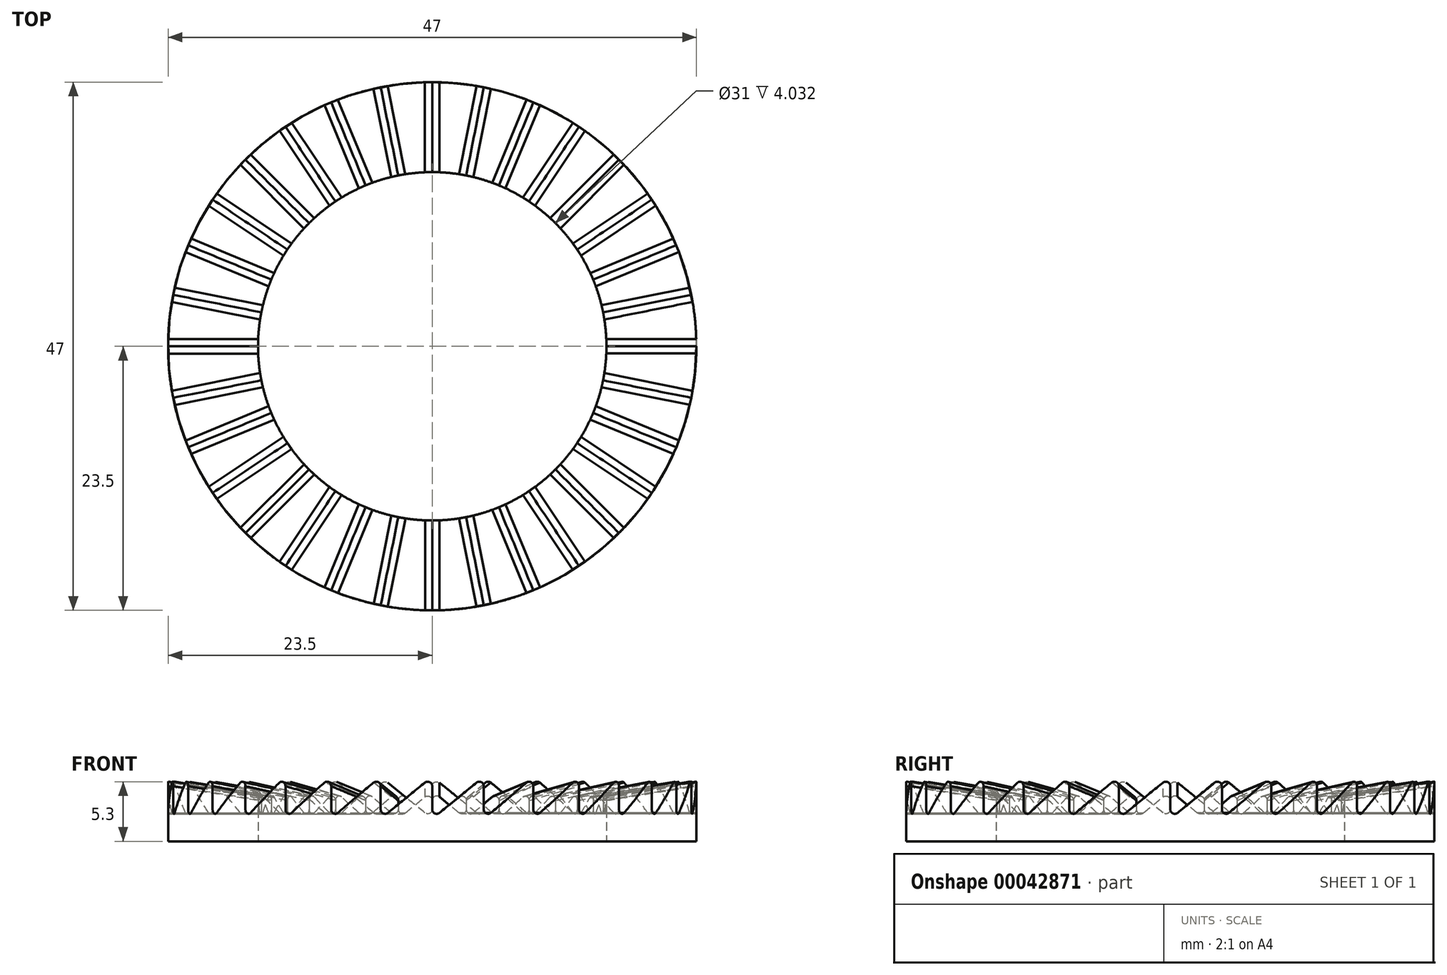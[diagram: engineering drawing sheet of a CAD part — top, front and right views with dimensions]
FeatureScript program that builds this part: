
annotation { "Feature Type Name" : "Feature", "Feature Type Description" : "" }
export const myFeature = defineFeature(function(context is Context, id is Id, definition is map)
    precondition{}
    {
        {
            var Q0;
            Q0=qCreatedBy(makeId("Top.planeOp"),FACE);
            var sketch = newSketch(context, id + "F0", { "sketchPlane" : qUnion([Q0])});
            skCircle(sketch, "E0", {"center": v(0, 0) * mm, "radius": 24 * mm});
            skCircle(sketch, "E1", {"center": v(0, 0) * mm, "radius": 25 * mm});
            skCircle(sketch, "E2", {"center": v(0, 0) * mm, "radius": 13 * mm});
            skCircle(sketch, "E3", {"center": v(0, 0) * mm, "radius": 15.5 * mm});
            skCircle(sketch, "E4", {"center": v(0, 0) * mm, "radius": 23.5 * mm});
            skCircle(sketch, "E5", {"center": v(0, 0) * mm, "radius": 12.5 * mm});
            skSolve(sketch);
        }
        {
            var Q0;
            Q0=makeQuery(id+"F0.imprint","IMPRINT",FACE,{"disambiguationData":[TD([[makeQuery(id+"F0.imprint","IMPRINT",EDGE,{"derivedFrom":sQuery(id+"F0.wireOp",EDGE,"E3")}),-1.0]])]});
            extrude(context, id + "F1", {"entities" : qUnion([Q0]), "depth" : 10 * mm});
        }
        {
            var Q0;
            Q0=qCreatedBy(makeId("Right.planeOp"),FACE);
            var sketch = newSketch(context, id + "F2", { "sketchPlane" : qUnion([Q0])});
            skLineSegment(sketch, "E6", {"start": v(0, 10) * mm, "end": v(0, 2) * mm});
            skLineSegment(sketch, "E7", {"start": v(0, 2) * mm, "end": v(9.8, 10) * mm});
            skLineSegment(sketch, "E8", {"start": v(0, 10) * mm, "end": v(9.8, 10) * mm});
            skSolve(sketch);
        }
        {
            var Q0;
            Q0=makeQuery(id+"F2.imprint","IMPRINT",FACE,{"disambiguationData":[TD([[makeQuery(id+"F2.imprint","IMPRINT",EDGE,{"derivedFrom":sQuery(id+"F2.wireOp",EDGE,"E6")}),1.0]])]});
            extrude(context, id + "F3", {"entities" : qUnion([Q0]), "depth" : 23.5 * mm});
        }
        {
            var Q0;
            Q0=makeQuery(id+"F3.opExtrude","SWEPT_BODY",BODY,{"disambiguationData":[OSD([sQuery(id+"F2.wireOp",EDGE,"E6"),sQuery(id+"F2.wireOp",EDGE,"E7"),sQuery(id+"F2.wireOp",EDGE,"E8")])]});
            var Q1;
            Q1=makeQuery(id+"F3.opExtrude","CAP_EDGE",EDGE,{"disambiguationData":[OSD([sQuery(id+"F2.wireOp",EDGE,"E6")])],"isStart":true});
            circularPattern(context, id + "F4", {"entities" : qUnion([Q0]), "axis" : qUnion([Q1]), "angle" : 11.25 * degree, "instanceCount" : round(32)});
        }
        {
            var Q0;
            Q0=makeQuery(id+"F3.opExtrude","SWEPT_BODY",BODY,{"disambiguationData":[OSD([sQuery(id+"F2.wireOp",EDGE,"E6"),sQuery(id+"F2.wireOp",EDGE,"E7"),sQuery(id+"F2.wireOp",EDGE,"E8")])]});
            var Q1;
            Q1=makeQuery(id+"F4.opPattern","COPY",BODY,{"derivedFrom":makeQuery(id+"F3.opExtrude","SWEPT_BODY",BODY,{"disambiguationData":[OSD([sQuery(id+"F2.wireOp",EDGE,"E6"),sQuery(id+"F2.wireOp",EDGE,"E7"),sQuery(id+"F2.wireOp",EDGE,"E8")])]}),"instanceName":"1"});
            var Q2;
            Q2=makeQuery(id+"F4.opPattern","COPY",BODY,{"derivedFrom":makeQuery(id+"F3.opExtrude","SWEPT_BODY",BODY,{"disambiguationData":[OSD([sQuery(id+"F2.wireOp",EDGE,"E6"),sQuery(id+"F2.wireOp",EDGE,"E7"),sQuery(id+"F2.wireOp",EDGE,"E8")])]}),"instanceName":"2"});
            var Q3;
            Q3=makeQuery(id+"F4.opPattern","COPY",BODY,{"derivedFrom":makeQuery(id+"F3.opExtrude","SWEPT_BODY",BODY,{"disambiguationData":[OSD([sQuery(id+"F2.wireOp",EDGE,"E6"),sQuery(id+"F2.wireOp",EDGE,"E7"),sQuery(id+"F2.wireOp",EDGE,"E8")])]}),"instanceName":"3"});
            var Q4;
            Q4=makeQuery(id+"F4.opPattern","COPY",BODY,{"derivedFrom":makeQuery(id+"F3.opExtrude","SWEPT_BODY",BODY,{"disambiguationData":[OSD([sQuery(id+"F2.wireOp",EDGE,"E6"),sQuery(id+"F2.wireOp",EDGE,"E7"),sQuery(id+"F2.wireOp",EDGE,"E8")])]}),"instanceName":"4"});
            var Q5;
            Q5=makeQuery(id+"F4.opPattern","COPY",BODY,{"derivedFrom":makeQuery(id+"F3.opExtrude","SWEPT_BODY",BODY,{"disambiguationData":[OSD([sQuery(id+"F2.wireOp",EDGE,"E6"),sQuery(id+"F2.wireOp",EDGE,"E7"),sQuery(id+"F2.wireOp",EDGE,"E8")])]}),"instanceName":"5"});
            var Q6;
            Q6=makeQuery(id+"F4.opPattern","COPY",BODY,{"derivedFrom":makeQuery(id+"F3.opExtrude","SWEPT_BODY",BODY,{"disambiguationData":[OSD([sQuery(id+"F2.wireOp",EDGE,"E6"),sQuery(id+"F2.wireOp",EDGE,"E7"),sQuery(id+"F2.wireOp",EDGE,"E8")])]}),"instanceName":"6"});
            var Q7;
            Q7=makeQuery(id+"F4.opPattern","COPY",BODY,{"derivedFrom":makeQuery(id+"F3.opExtrude","SWEPT_BODY",BODY,{"disambiguationData":[OSD([sQuery(id+"F2.wireOp",EDGE,"E6"),sQuery(id+"F2.wireOp",EDGE,"E7"),sQuery(id+"F2.wireOp",EDGE,"E8")])]}),"instanceName":"7"});
            var Q8;
            Q8=makeQuery(id+"F4.opPattern","COPY",BODY,{"derivedFrom":makeQuery(id+"F3.opExtrude","SWEPT_BODY",BODY,{"disambiguationData":[OSD([sQuery(id+"F2.wireOp",EDGE,"E6"),sQuery(id+"F2.wireOp",EDGE,"E7"),sQuery(id+"F2.wireOp",EDGE,"E8")])]}),"instanceName":"8"});
            var Q9;
            Q9=makeQuery(id+"F4.opPattern","COPY",BODY,{"derivedFrom":makeQuery(id+"F3.opExtrude","SWEPT_BODY",BODY,{"disambiguationData":[OSD([sQuery(id+"F2.wireOp",EDGE,"E6"),sQuery(id+"F2.wireOp",EDGE,"E7"),sQuery(id+"F2.wireOp",EDGE,"E8")])]}),"instanceName":"9"});
            var Q10;
            Q10=makeQuery(id+"F4.opPattern","COPY",BODY,{"derivedFrom":makeQuery(id+"F3.opExtrude","SWEPT_BODY",BODY,{"disambiguationData":[OSD([sQuery(id+"F2.wireOp",EDGE,"E6"),sQuery(id+"F2.wireOp",EDGE,"E7"),sQuery(id+"F2.wireOp",EDGE,"E8")])]}),"instanceName":"10"});
            var Q11;
            Q11=makeQuery(id+"F4.opPattern","COPY",BODY,{"derivedFrom":makeQuery(id+"F3.opExtrude","SWEPT_BODY",BODY,{"disambiguationData":[OSD([sQuery(id+"F2.wireOp",EDGE,"E6"),sQuery(id+"F2.wireOp",EDGE,"E7"),sQuery(id+"F2.wireOp",EDGE,"E8")])]}),"instanceName":"11"});
            var Q12;
            Q12=makeQuery(id+"F4.opPattern","COPY",BODY,{"derivedFrom":makeQuery(id+"F3.opExtrude","SWEPT_BODY",BODY,{"disambiguationData":[OSD([sQuery(id+"F2.wireOp",EDGE,"E6"),sQuery(id+"F2.wireOp",EDGE,"E7"),sQuery(id+"F2.wireOp",EDGE,"E8")])]}),"instanceName":"12"});
            var Q13;
            Q13=makeQuery(id+"F4.opPattern","COPY",BODY,{"derivedFrom":makeQuery(id+"F3.opExtrude","SWEPT_BODY",BODY,{"disambiguationData":[OSD([sQuery(id+"F2.wireOp",EDGE,"E6"),sQuery(id+"F2.wireOp",EDGE,"E7"),sQuery(id+"F2.wireOp",EDGE,"E8")])]}),"instanceName":"13"});
            var Q14;
            Q14=makeQuery(id+"F4.opPattern","COPY",BODY,{"derivedFrom":makeQuery(id+"F3.opExtrude","SWEPT_BODY",BODY,{"disambiguationData":[OSD([sQuery(id+"F2.wireOp",EDGE,"E6"),sQuery(id+"F2.wireOp",EDGE,"E7"),sQuery(id+"F2.wireOp",EDGE,"E8")])]}),"instanceName":"14"});
            var Q15;
            Q15=makeQuery(id+"F4.opPattern","COPY",BODY,{"derivedFrom":makeQuery(id+"F3.opExtrude","SWEPT_BODY",BODY,{"disambiguationData":[OSD([sQuery(id+"F2.wireOp",EDGE,"E6"),sQuery(id+"F2.wireOp",EDGE,"E7"),sQuery(id+"F2.wireOp",EDGE,"E8")])]}),"instanceName":"15"});
            var Q16;
            Q16=makeQuery(id+"F4.opPattern","COPY",BODY,{"derivedFrom":makeQuery(id+"F3.opExtrude","SWEPT_BODY",BODY,{"disambiguationData":[OSD([sQuery(id+"F2.wireOp",EDGE,"E6"),sQuery(id+"F2.wireOp",EDGE,"E7"),sQuery(id+"F2.wireOp",EDGE,"E8")])]}),"instanceName":"16"});
            var Q17;
            Q17=makeQuery(id+"F4.opPattern","COPY",BODY,{"derivedFrom":makeQuery(id+"F3.opExtrude","SWEPT_BODY",BODY,{"disambiguationData":[OSD([sQuery(id+"F2.wireOp",EDGE,"E6"),sQuery(id+"F2.wireOp",EDGE,"E7"),sQuery(id+"F2.wireOp",EDGE,"E8")])]}),"instanceName":"17"});
            var Q18;
            Q18=makeQuery(id+"F4.opPattern","COPY",BODY,{"derivedFrom":makeQuery(id+"F3.opExtrude","SWEPT_BODY",BODY,{"disambiguationData":[OSD([sQuery(id+"F2.wireOp",EDGE,"E6"),sQuery(id+"F2.wireOp",EDGE,"E7"),sQuery(id+"F2.wireOp",EDGE,"E8")])]}),"instanceName":"18"});
            var Q19;
            Q19=makeQuery(id+"F4.opPattern","COPY",BODY,{"derivedFrom":makeQuery(id+"F3.opExtrude","SWEPT_BODY",BODY,{"disambiguationData":[OSD([sQuery(id+"F2.wireOp",EDGE,"E6"),sQuery(id+"F2.wireOp",EDGE,"E7"),sQuery(id+"F2.wireOp",EDGE,"E8")])]}),"instanceName":"19"});
            var Q20;
            Q20=makeQuery(id+"F4.opPattern","COPY",BODY,{"derivedFrom":makeQuery(id+"F3.opExtrude","SWEPT_BODY",BODY,{"disambiguationData":[OSD([sQuery(id+"F2.wireOp",EDGE,"E6"),sQuery(id+"F2.wireOp",EDGE,"E7"),sQuery(id+"F2.wireOp",EDGE,"E8")])]}),"instanceName":"20"});
            var Q21;
            Q21=makeQuery(id+"F4.opPattern","COPY",BODY,{"derivedFrom":makeQuery(id+"F3.opExtrude","SWEPT_BODY",BODY,{"disambiguationData":[OSD([sQuery(id+"F2.wireOp",EDGE,"E6"),sQuery(id+"F2.wireOp",EDGE,"E7"),sQuery(id+"F2.wireOp",EDGE,"E8")])]}),"instanceName":"21"});
            var Q22;
            Q22=makeQuery(id+"F4.opPattern","COPY",BODY,{"derivedFrom":makeQuery(id+"F3.opExtrude","SWEPT_BODY",BODY,{"disambiguationData":[OSD([sQuery(id+"F2.wireOp",EDGE,"E6"),sQuery(id+"F2.wireOp",EDGE,"E7"),sQuery(id+"F2.wireOp",EDGE,"E8")])]}),"instanceName":"22"});
            var Q23;
            Q23=makeQuery(id+"F4.opPattern","COPY",BODY,{"derivedFrom":makeQuery(id+"F3.opExtrude","SWEPT_BODY",BODY,{"disambiguationData":[OSD([sQuery(id+"F2.wireOp",EDGE,"E6"),sQuery(id+"F2.wireOp",EDGE,"E7"),sQuery(id+"F2.wireOp",EDGE,"E8")])]}),"instanceName":"23"});
            var Q24;
            Q24=makeQuery(id+"F4.opPattern","COPY",BODY,{"derivedFrom":makeQuery(id+"F3.opExtrude","SWEPT_BODY",BODY,{"disambiguationData":[OSD([sQuery(id+"F2.wireOp",EDGE,"E6"),sQuery(id+"F2.wireOp",EDGE,"E7"),sQuery(id+"F2.wireOp",EDGE,"E8")])]}),"instanceName":"24"});
            var Q25;
            Q25=makeQuery(id+"F4.opPattern","COPY",BODY,{"derivedFrom":makeQuery(id+"F3.opExtrude","SWEPT_BODY",BODY,{"disambiguationData":[OSD([sQuery(id+"F2.wireOp",EDGE,"E6"),sQuery(id+"F2.wireOp",EDGE,"E7"),sQuery(id+"F2.wireOp",EDGE,"E8")])]}),"instanceName":"25"});
            var Q26;
            Q26=makeQuery(id+"F4.opPattern","COPY",BODY,{"derivedFrom":makeQuery(id+"F3.opExtrude","SWEPT_BODY",BODY,{"disambiguationData":[OSD([sQuery(id+"F2.wireOp",EDGE,"E6"),sQuery(id+"F2.wireOp",EDGE,"E7"),sQuery(id+"F2.wireOp",EDGE,"E8")])]}),"instanceName":"26"});
            var Q27;
            Q27=makeQuery(id+"F4.opPattern","COPY",BODY,{"derivedFrom":makeQuery(id+"F3.opExtrude","SWEPT_BODY",BODY,{"disambiguationData":[OSD([sQuery(id+"F2.wireOp",EDGE,"E6"),sQuery(id+"F2.wireOp",EDGE,"E7"),sQuery(id+"F2.wireOp",EDGE,"E8")])]}),"instanceName":"27"});
            var Q28;
            Q28=makeQuery(id+"F4.opPattern","COPY",BODY,{"derivedFrom":makeQuery(id+"F3.opExtrude","SWEPT_BODY",BODY,{"disambiguationData":[OSD([sQuery(id+"F2.wireOp",EDGE,"E6"),sQuery(id+"F2.wireOp",EDGE,"E7"),sQuery(id+"F2.wireOp",EDGE,"E8")])]}),"instanceName":"28"});
            var Q29;
            Q29=makeQuery(id+"F4.opPattern","COPY",BODY,{"derivedFrom":makeQuery(id+"F3.opExtrude","SWEPT_BODY",BODY,{"disambiguationData":[OSD([sQuery(id+"F2.wireOp",EDGE,"E6"),sQuery(id+"F2.wireOp",EDGE,"E7"),sQuery(id+"F2.wireOp",EDGE,"E8")])]}),"instanceName":"29"});
            var Q30;
            Q30=makeQuery(id+"F4.opPattern","COPY",BODY,{"derivedFrom":makeQuery(id+"F3.opExtrude","SWEPT_BODY",BODY,{"disambiguationData":[OSD([sQuery(id+"F2.wireOp",EDGE,"E6"),sQuery(id+"F2.wireOp",EDGE,"E7"),sQuery(id+"F2.wireOp",EDGE,"E8")])]}),"instanceName":"30"});
            var Q31;
            Q31=makeQuery(id+"F4.opPattern","COPY",BODY,{"derivedFrom":makeQuery(id+"F3.opExtrude","SWEPT_BODY",BODY,{"disambiguationData":[OSD([sQuery(id+"F2.wireOp",EDGE,"E6"),sQuery(id+"F2.wireOp",EDGE,"E7"),sQuery(id+"F2.wireOp",EDGE,"E8")])]}),"instanceName":"31"});
            booleanBodies(context, id + "F5", {"operationType" : BooleanOperationType.UNION, "tools" : qUnion([Q0, Q1, Q2, Q3, Q4, Q5, Q6, Q7, Q8, Q9, Q10, Q11, Q12, Q13, Q14, Q15, Q16, Q17, Q18, Q19, Q20, Q21, Q22, Q23, Q24, Q25, Q26, Q27, Q28, Q29, Q30, Q31])});
        }
        {
            var Q0;
            Q0=makeQuery(id+"F3.opExtrude","SWEPT_BODY",BODY,{"disambiguationData":[OSD([sQuery(id+"F2.wireOp",EDGE,"E6"),sQuery(id+"F2.wireOp",EDGE,"E7"),sQuery(id+"F2.wireOp",EDGE,"E8")])]});
            var Q1;
            Q1=makeQuery(id+"F1.opExtrude","SWEPT_BODY",BODY,{"disambiguationData":[OSD([sQuery(id+"F0.wireOp",EDGE,"E3"),sQuery(id+"F0.wireOp",EDGE,"E4")])]});
            booleanBodies(context, id + "F6", {"operationType" : BooleanOperationType.SUBTRACTION, "tools" : qUnion([Q0]), "targets" : qUnion([Q1])});
        }
        {
            var Q0;
            Q0=makeQuery(id+"F6.opBoolean","COPY",EDGE,{"derivedFrom":makeQuery(id+"F4.opPattern","COPY",EDGE,{"derivedFrom":makeQuery(id+"F3.opExtrude","SWEPT_EDGE",EDGE,{"disambiguationData":[OSD([sQuery(id+"F2.wireOp",EDGE,"E6"),sQuery(id+"F2.wireOp",EDGE,"E7")])]}),"instanceName":"6"})});
            var Q1;
            Q1=makeQuery(id+"F6.opBoolean","COPY",EDGE,{"derivedFrom":makeQuery(id+"F5.opBoolean","INTERSECT",EDGE,{"derivedFrom":[makeQuery(id+"F4.opPattern","COPY",FACE,{"derivedFrom":makeQuery(id+"F3.opExtrude","SWEPT_FACE",FACE,{"disambiguationData":[OSD([sQuery(id+"F2.wireOp",EDGE,"E6")])]}),"instanceName":"5"}),makeQuery(id+"F4.opPattern","COPY",FACE,{"derivedFrom":makeQuery(id+"F3.opExtrude","SWEPT_FACE",FACE,{"disambiguationData":[OSD([sQuery(id+"F2.wireOp",EDGE,"E7")])]}),"instanceName":"6"})]})});
            var Q2;
            Q2=makeQuery(id+"F6.opBoolean","COPY",EDGE,{"derivedFrom":makeQuery(id+"F4.opPattern","COPY",EDGE,{"derivedFrom":makeQuery(id+"F3.opExtrude","SWEPT_EDGE",EDGE,{"disambiguationData":[OSD([sQuery(id+"F2.wireOp",EDGE,"E6"),sQuery(id+"F2.wireOp",EDGE,"E7")])]}),"instanceName":"5"})});
            var Q3;
            Q3=makeQuery(id+"F6.opBoolean","COPY",EDGE,{"derivedFrom":makeQuery(id+"F5.opBoolean","INTERSECT",EDGE,{"derivedFrom":[makeQuery(id+"F4.opPattern","COPY",FACE,{"derivedFrom":makeQuery(id+"F3.opExtrude","SWEPT_FACE",FACE,{"disambiguationData":[OSD([sQuery(id+"F2.wireOp",EDGE,"E6")])]}),"instanceName":"4"}),makeQuery(id+"F4.opPattern","COPY",FACE,{"derivedFrom":makeQuery(id+"F3.opExtrude","SWEPT_FACE",FACE,{"disambiguationData":[OSD([sQuery(id+"F2.wireOp",EDGE,"E7")])]}),"instanceName":"5"})]})});
            var Q4;
            Q4=makeQuery(id+"F6.opBoolean","COPY",EDGE,{"derivedFrom":makeQuery(id+"F4.opPattern","COPY",EDGE,{"derivedFrom":makeQuery(id+"F3.opExtrude","SWEPT_EDGE",EDGE,{"disambiguationData":[OSD([sQuery(id+"F2.wireOp",EDGE,"E6"),sQuery(id+"F2.wireOp",EDGE,"E7")])]}),"instanceName":"4"})});
            var Q5;
            Q5=makeQuery(id+"F6.opBoolean","COPY",EDGE,{"derivedFrom":makeQuery(id+"F5.opBoolean","INTERSECT",EDGE,{"derivedFrom":[makeQuery(id+"F4.opPattern","COPY",FACE,{"derivedFrom":makeQuery(id+"F3.opExtrude","SWEPT_FACE",FACE,{"disambiguationData":[OSD([sQuery(id+"F2.wireOp",EDGE,"E6")])]}),"instanceName":"3"}),makeQuery(id+"F4.opPattern","COPY",FACE,{"derivedFrom":makeQuery(id+"F3.opExtrude","SWEPT_FACE",FACE,{"disambiguationData":[OSD([sQuery(id+"F2.wireOp",EDGE,"E7")])]}),"instanceName":"4"})]})});
            var Q6;
            Q6=makeQuery(id+"F6.opBoolean","COPY",EDGE,{"derivedFrom":makeQuery(id+"F4.opPattern","COPY",EDGE,{"derivedFrom":makeQuery(id+"F3.opExtrude","SWEPT_EDGE",EDGE,{"disambiguationData":[OSD([sQuery(id+"F2.wireOp",EDGE,"E6"),sQuery(id+"F2.wireOp",EDGE,"E7")])]}),"instanceName":"3"})});
            var Q7;
            Q7=makeQuery(id+"F6.opBoolean","COPY",EDGE,{"derivedFrom":makeQuery(id+"F5.opBoolean","INTERSECT",EDGE,{"derivedFrom":[makeQuery(id+"F4.opPattern","COPY",FACE,{"derivedFrom":makeQuery(id+"F3.opExtrude","SWEPT_FACE",FACE,{"disambiguationData":[OSD([sQuery(id+"F2.wireOp",EDGE,"E6")])]}),"instanceName":"2"}),makeQuery(id+"F4.opPattern","COPY",FACE,{"derivedFrom":makeQuery(id+"F3.opExtrude","SWEPT_FACE",FACE,{"disambiguationData":[OSD([sQuery(id+"F2.wireOp",EDGE,"E7")])]}),"instanceName":"3"})]})});
            var Q8;
            Q8=makeQuery(id+"F6.opBoolean","COPY",EDGE,{"derivedFrom":makeQuery(id+"F4.opPattern","COPY",EDGE,{"derivedFrom":makeQuery(id+"F3.opExtrude","SWEPT_EDGE",EDGE,{"disambiguationData":[OSD([sQuery(id+"F2.wireOp",EDGE,"E6"),sQuery(id+"F2.wireOp",EDGE,"E7")])]}),"instanceName":"2"})});
            var Q9;
            Q9=makeQuery(id+"F6.opBoolean","COPY",EDGE,{"derivedFrom":makeQuery(id+"F5.opBoolean","INTERSECT",EDGE,{"derivedFrom":[makeQuery(id+"F4.opPattern","COPY",FACE,{"derivedFrom":makeQuery(id+"F3.opExtrude","SWEPT_FACE",FACE,{"disambiguationData":[OSD([sQuery(id+"F2.wireOp",EDGE,"E6")])]}),"instanceName":"1"}),makeQuery(id+"F4.opPattern","COPY",FACE,{"derivedFrom":makeQuery(id+"F3.opExtrude","SWEPT_FACE",FACE,{"disambiguationData":[OSD([sQuery(id+"F2.wireOp",EDGE,"E7")])]}),"instanceName":"2"})]})});
            var Q10;
            Q10=makeQuery(id+"F6.opBoolean","COPY",EDGE,{"derivedFrom":makeQuery(id+"F4.opPattern","COPY",EDGE,{"derivedFrom":makeQuery(id+"F3.opExtrude","SWEPT_EDGE",EDGE,{"disambiguationData":[OSD([sQuery(id+"F2.wireOp",EDGE,"E6"),sQuery(id+"F2.wireOp",EDGE,"E7")])]}),"instanceName":"1"})});
            var Q11;
            Q11=makeQuery(id+"F6.opBoolean","COPY",EDGE,{"derivedFrom":makeQuery(id+"F3.opExtrude","SWEPT_EDGE",EDGE,{"disambiguationData":[OSD([sQuery(id+"F2.wireOp",EDGE,"E6"),sQuery(id+"F2.wireOp",EDGE,"E7")])]})});
            var Q12;
            Q12=makeQuery(id+"F6.opBoolean","COPY",EDGE,{"derivedFrom":makeQuery(id+"F5.opBoolean","INTERSECT",EDGE,{"derivedFrom":[makeQuery(id+"F3.opExtrude","SWEPT_FACE",FACE,{"disambiguationData":[OSD([sQuery(id+"F2.wireOp",EDGE,"E6")])]}),makeQuery(id+"F4.opPattern","COPY",FACE,{"derivedFrom":makeQuery(id+"F3.opExtrude","SWEPT_FACE",FACE,{"disambiguationData":[OSD([sQuery(id+"F2.wireOp",EDGE,"E7")])]}),"instanceName":"1"})]})});
            var Q13;
            {var subQ0=sQuery(id+"F2.wireOp",EDGE,"E7");var subQ1=sQuery(id+"F2.wireOp",EDGE,"E6");Q13=makeQuery(id+"F6.opBoolean","COPY",EDGE,{"derivedFrom":makeQuery(id+"F5.opBoolean","INTERSECT",EDGE,{"derivedFrom":[makeQuery(id+"F3.opExtrude","SWEPT_FACE",FACE,{"disambiguationData":[OSD([subQ0])]}),makeQuery(id+"F4.opPattern","COPY",FACE,{"derivedFrom":makeQuery(id+"F3.opExtrude","CAP_FACE",FACE,{"disambiguationData":[OSD([subQ1,subQ0,sQuery(id+"F2.wireOp",EDGE,"E8")])],"isStart":true}),"instanceName":"23"}),makeQuery(id+"F4.opPattern","COPY",FACE,{"derivedFrom":makeQuery(id+"F3.opExtrude","SWEPT_FACE",FACE,{"disambiguationData":[OSD([subQ1])]}),"instanceName":"31"})]})});}
            var Q14;
            Q14=makeQuery(id+"F6.opBoolean","COPY",EDGE,{"derivedFrom":makeQuery(id+"F4.opPattern","COPY",EDGE,{"derivedFrom":makeQuery(id+"F3.opExtrude","SWEPT_EDGE",EDGE,{"disambiguationData":[OSD([sQuery(id+"F2.wireOp",EDGE,"E6"),sQuery(id+"F2.wireOp",EDGE,"E7")])]}),"instanceName":"31"})});
            var Q15;
            Q15=makeQuery(id+"F6.opBoolean","COPY",EDGE,{"derivedFrom":makeQuery(id+"F5.opBoolean","INTERSECT",EDGE,{"derivedFrom":[makeQuery(id+"F4.opPattern","COPY",FACE,{"derivedFrom":makeQuery(id+"F3.opExtrude","SWEPT_FACE",FACE,{"disambiguationData":[OSD([sQuery(id+"F2.wireOp",EDGE,"E6")])]}),"instanceName":"30"}),makeQuery(id+"F4.opPattern","COPY",FACE,{"derivedFrom":makeQuery(id+"F3.opExtrude","SWEPT_FACE",FACE,{"disambiguationData":[OSD([sQuery(id+"F2.wireOp",EDGE,"E7")])]}),"instanceName":"31"})]})});
            var Q16;
            Q16=makeQuery(id+"F6.opBoolean","COPY",EDGE,{"derivedFrom":makeQuery(id+"F5.opBoolean","INTERSECT",EDGE,{"derivedFrom":[makeQuery(id+"F4.opPattern","COPY",FACE,{"derivedFrom":makeQuery(id+"F3.opExtrude","SWEPT_FACE",FACE,{"disambiguationData":[OSD([sQuery(id+"F2.wireOp",EDGE,"E6")])]}),"instanceName":"29"}),makeQuery(id+"F4.opPattern","COPY",FACE,{"derivedFrom":makeQuery(id+"F3.opExtrude","SWEPT_FACE",FACE,{"disambiguationData":[OSD([sQuery(id+"F2.wireOp",EDGE,"E7")])]}),"instanceName":"30"})]})});
            var Q17;
            Q17=makeQuery(id+"F6.opBoolean","COPY",EDGE,{"derivedFrom":makeQuery(id+"F4.opPattern","COPY",EDGE,{"derivedFrom":makeQuery(id+"F3.opExtrude","SWEPT_EDGE",EDGE,{"disambiguationData":[OSD([sQuery(id+"F2.wireOp",EDGE,"E6"),sQuery(id+"F2.wireOp",EDGE,"E7")])]}),"instanceName":"29"})});
            var Q18;
            Q18=makeQuery(id+"F6.opBoolean","COPY",EDGE,{"derivedFrom":makeQuery(id+"F4.opPattern","COPY",EDGE,{"derivedFrom":makeQuery(id+"F3.opExtrude","SWEPT_EDGE",EDGE,{"disambiguationData":[OSD([sQuery(id+"F2.wireOp",EDGE,"E6"),sQuery(id+"F2.wireOp",EDGE,"E7")])]}),"instanceName":"30"})});
            var Q19;
            Q19=makeQuery(id+"F6.opBoolean","COPY",EDGE,{"derivedFrom":makeQuery(id+"F5.opBoolean","INTERSECT",EDGE,{"derivedFrom":[makeQuery(id+"F4.opPattern","COPY",FACE,{"derivedFrom":makeQuery(id+"F3.opExtrude","SWEPT_FACE",FACE,{"disambiguationData":[OSD([sQuery(id+"F2.wireOp",EDGE,"E6")])]}),"instanceName":"28"}),makeQuery(id+"F4.opPattern","COPY",FACE,{"derivedFrom":makeQuery(id+"F3.opExtrude","SWEPT_FACE",FACE,{"disambiguationData":[OSD([sQuery(id+"F2.wireOp",EDGE,"E7")])]}),"instanceName":"29"})]})});
            var Q20;
            Q20=makeQuery(id+"F6.opBoolean","COPY",EDGE,{"derivedFrom":makeQuery(id+"F4.opPattern","COPY",EDGE,{"derivedFrom":makeQuery(id+"F3.opExtrude","SWEPT_EDGE",EDGE,{"disambiguationData":[OSD([sQuery(id+"F2.wireOp",EDGE,"E6"),sQuery(id+"F2.wireOp",EDGE,"E7")])]}),"instanceName":"28"})});
            var Q21;
            Q21=makeQuery(id+"F6.opBoolean","COPY",EDGE,{"derivedFrom":makeQuery(id+"F5.opBoolean","INTERSECT",EDGE,{"derivedFrom":[makeQuery(id+"F4.opPattern","COPY",FACE,{"derivedFrom":makeQuery(id+"F3.opExtrude","SWEPT_FACE",FACE,{"disambiguationData":[OSD([sQuery(id+"F2.wireOp",EDGE,"E6")])]}),"instanceName":"27"}),makeQuery(id+"F4.opPattern","COPY",FACE,{"derivedFrom":makeQuery(id+"F3.opExtrude","SWEPT_FACE",FACE,{"disambiguationData":[OSD([sQuery(id+"F2.wireOp",EDGE,"E7")])]}),"instanceName":"28"})]})});
            var Q22;
            Q22=makeQuery(id+"F6.opBoolean","COPY",EDGE,{"derivedFrom":makeQuery(id+"F4.opPattern","COPY",EDGE,{"derivedFrom":makeQuery(id+"F3.opExtrude","SWEPT_EDGE",EDGE,{"disambiguationData":[OSD([sQuery(id+"F2.wireOp",EDGE,"E6"),sQuery(id+"F2.wireOp",EDGE,"E7")])]}),"instanceName":"27"})});
            var Q23;
            Q23=makeQuery(id+"F6.opBoolean","COPY",EDGE,{"derivedFrom":makeQuery(id+"F5.opBoolean","INTERSECT",EDGE,{"derivedFrom":[makeQuery(id+"F4.opPattern","COPY",FACE,{"derivedFrom":makeQuery(id+"F3.opExtrude","SWEPT_FACE",FACE,{"disambiguationData":[OSD([sQuery(id+"F2.wireOp",EDGE,"E6")])]}),"instanceName":"26"}),makeQuery(id+"F4.opPattern","COPY",FACE,{"derivedFrom":makeQuery(id+"F3.opExtrude","SWEPT_FACE",FACE,{"disambiguationData":[OSD([sQuery(id+"F2.wireOp",EDGE,"E7")])]}),"instanceName":"27"})]})});
            var Q24;
            Q24=makeQuery(id+"F6.opBoolean","COPY",EDGE,{"derivedFrom":makeQuery(id+"F4.opPattern","COPY",EDGE,{"derivedFrom":makeQuery(id+"F3.opExtrude","SWEPT_EDGE",EDGE,{"disambiguationData":[OSD([sQuery(id+"F2.wireOp",EDGE,"E6"),sQuery(id+"F2.wireOp",EDGE,"E7")])]}),"instanceName":"26"})});
            var Q25;
            Q25=makeQuery(id+"F6.opBoolean","COPY",EDGE,{"derivedFrom":makeQuery(id+"F5.opBoolean","INTERSECT",EDGE,{"derivedFrom":[makeQuery(id+"F4.opPattern","COPY",FACE,{"derivedFrom":makeQuery(id+"F3.opExtrude","SWEPT_FACE",FACE,{"disambiguationData":[OSD([sQuery(id+"F2.wireOp",EDGE,"E6")])]}),"instanceName":"25"}),makeQuery(id+"F4.opPattern","COPY",FACE,{"derivedFrom":makeQuery(id+"F3.opExtrude","SWEPT_FACE",FACE,{"disambiguationData":[OSD([sQuery(id+"F2.wireOp",EDGE,"E7")])]}),"instanceName":"26"})]})});
            var Q26;
            Q26=makeQuery(id+"F6.opBoolean","COPY",EDGE,{"derivedFrom":makeQuery(id+"F4.opPattern","COPY",EDGE,{"derivedFrom":makeQuery(id+"F3.opExtrude","SWEPT_EDGE",EDGE,{"disambiguationData":[OSD([sQuery(id+"F2.wireOp",EDGE,"E6"),sQuery(id+"F2.wireOp",EDGE,"E7")])]}),"instanceName":"25"})});
            var Q27;
            Q27=makeQuery(id+"F6.opBoolean","COPY",EDGE,{"derivedFrom":makeQuery(id+"F5.opBoolean","INTERSECT",EDGE,{"derivedFrom":[makeQuery(id+"F4.opPattern","COPY",FACE,{"derivedFrom":makeQuery(id+"F3.opExtrude","SWEPT_FACE",FACE,{"disambiguationData":[OSD([sQuery(id+"F2.wireOp",EDGE,"E6")])]}),"instanceName":"24"}),makeQuery(id+"F4.opPattern","COPY",FACE,{"derivedFrom":makeQuery(id+"F3.opExtrude","SWEPT_FACE",FACE,{"disambiguationData":[OSD([sQuery(id+"F2.wireOp",EDGE,"E7")])]}),"instanceName":"25"})]})});
            var Q28;
            Q28=makeQuery(id+"F6.opBoolean","COPY",EDGE,{"derivedFrom":makeQuery(id+"F4.opPattern","COPY",EDGE,{"derivedFrom":makeQuery(id+"F3.opExtrude","SWEPT_EDGE",EDGE,{"disambiguationData":[OSD([sQuery(id+"F2.wireOp",EDGE,"E6"),sQuery(id+"F2.wireOp",EDGE,"E7")])]}),"instanceName":"24"})});
            var Q29;
            Q29=makeQuery(id+"F6.opBoolean","COPY",EDGE,{"derivedFrom":makeQuery(id+"F5.opBoolean","INTERSECT",EDGE,{"derivedFrom":[makeQuery(id+"F4.opPattern","COPY",FACE,{"derivedFrom":makeQuery(id+"F3.opExtrude","SWEPT_FACE",FACE,{"disambiguationData":[OSD([sQuery(id+"F2.wireOp",EDGE,"E6")])]}),"instanceName":"23"}),makeQuery(id+"F4.opPattern","COPY",FACE,{"derivedFrom":makeQuery(id+"F3.opExtrude","SWEPT_FACE",FACE,{"disambiguationData":[OSD([sQuery(id+"F2.wireOp",EDGE,"E7")])]}),"instanceName":"24"})]})});
            var Q30;
            Q30=makeQuery(id+"F6.opBoolean","COPY",EDGE,{"derivedFrom":makeQuery(id+"F4.opPattern","COPY",EDGE,{"derivedFrom":makeQuery(id+"F3.opExtrude","SWEPT_EDGE",EDGE,{"disambiguationData":[OSD([sQuery(id+"F2.wireOp",EDGE,"E6"),sQuery(id+"F2.wireOp",EDGE,"E7")])]}),"instanceName":"23"})});
            var Q31;
            Q31=makeQuery(id+"F6.opBoolean","COPY",EDGE,{"derivedFrom":makeQuery(id+"F5.opBoolean","INTERSECT",EDGE,{"derivedFrom":[makeQuery(id+"F4.opPattern","COPY",FACE,{"derivedFrom":makeQuery(id+"F3.opExtrude","SWEPT_FACE",FACE,{"disambiguationData":[OSD([sQuery(id+"F2.wireOp",EDGE,"E6")])]}),"instanceName":"22"}),makeQuery(id+"F4.opPattern","COPY",FACE,{"derivedFrom":makeQuery(id+"F3.opExtrude","SWEPT_FACE",FACE,{"disambiguationData":[OSD([sQuery(id+"F2.wireOp",EDGE,"E7")])]}),"instanceName":"23"})]})});
            var Q32;
            Q32=makeQuery(id+"F6.opBoolean","COPY",EDGE,{"derivedFrom":makeQuery(id+"F4.opPattern","COPY",EDGE,{"derivedFrom":makeQuery(id+"F3.opExtrude","SWEPT_EDGE",EDGE,{"disambiguationData":[OSD([sQuery(id+"F2.wireOp",EDGE,"E6"),sQuery(id+"F2.wireOp",EDGE,"E7")])]}),"instanceName":"22"})});
            var Q33;
            Q33=makeQuery(id+"F6.opBoolean","COPY",EDGE,{"derivedFrom":makeQuery(id+"F5.opBoolean","INTERSECT",EDGE,{"derivedFrom":[makeQuery(id+"F4.opPattern","COPY",FACE,{"derivedFrom":makeQuery(id+"F3.opExtrude","SWEPT_FACE",FACE,{"disambiguationData":[OSD([sQuery(id+"F2.wireOp",EDGE,"E6")])]}),"instanceName":"21"}),makeQuery(id+"F4.opPattern","COPY",FACE,{"derivedFrom":makeQuery(id+"F3.opExtrude","SWEPT_FACE",FACE,{"disambiguationData":[OSD([sQuery(id+"F2.wireOp",EDGE,"E7")])]}),"instanceName":"22"})]})});
            var Q34;
            Q34=makeQuery(id+"F6.opBoolean","COPY",EDGE,{"derivedFrom":makeQuery(id+"F4.opPattern","COPY",EDGE,{"derivedFrom":makeQuery(id+"F3.opExtrude","SWEPT_EDGE",EDGE,{"disambiguationData":[OSD([sQuery(id+"F2.wireOp",EDGE,"E6"),sQuery(id+"F2.wireOp",EDGE,"E7")])]}),"instanceName":"21"})});
            var Q35;
            Q35=makeQuery(id+"F6.opBoolean","COPY",EDGE,{"derivedFrom":makeQuery(id+"F5.opBoolean","INTERSECT",EDGE,{"derivedFrom":[makeQuery(id+"F4.opPattern","COPY",FACE,{"derivedFrom":makeQuery(id+"F3.opExtrude","SWEPT_FACE",FACE,{"disambiguationData":[OSD([sQuery(id+"F2.wireOp",EDGE,"E6")])]}),"instanceName":"20"}),makeQuery(id+"F4.opPattern","COPY",FACE,{"derivedFrom":makeQuery(id+"F3.opExtrude","SWEPT_FACE",FACE,{"disambiguationData":[OSD([sQuery(id+"F2.wireOp",EDGE,"E7")])]}),"instanceName":"21"})]})});
            var Q36;
            Q36=makeQuery(id+"F6.opBoolean","COPY",EDGE,{"derivedFrom":makeQuery(id+"F4.opPattern","COPY",EDGE,{"derivedFrom":makeQuery(id+"F3.opExtrude","SWEPT_EDGE",EDGE,{"disambiguationData":[OSD([sQuery(id+"F2.wireOp",EDGE,"E6"),sQuery(id+"F2.wireOp",EDGE,"E7")])]}),"instanceName":"20"})});
            var Q37;
            Q37=makeQuery(id+"F6.opBoolean","COPY",EDGE,{"derivedFrom":makeQuery(id+"F5.opBoolean","INTERSECT",EDGE,{"derivedFrom":[makeQuery(id+"F4.opPattern","COPY",FACE,{"derivedFrom":makeQuery(id+"F3.opExtrude","SWEPT_FACE",FACE,{"disambiguationData":[OSD([sQuery(id+"F2.wireOp",EDGE,"E6")])]}),"instanceName":"19"}),makeQuery(id+"F4.opPattern","COPY",FACE,{"derivedFrom":makeQuery(id+"F3.opExtrude","SWEPT_FACE",FACE,{"disambiguationData":[OSD([sQuery(id+"F2.wireOp",EDGE,"E7")])]}),"instanceName":"20"})]})});
            var Q38;
            Q38=makeQuery(id+"F6.opBoolean","COPY",EDGE,{"derivedFrom":makeQuery(id+"F4.opPattern","COPY",EDGE,{"derivedFrom":makeQuery(id+"F3.opExtrude","SWEPT_EDGE",EDGE,{"disambiguationData":[OSD([sQuery(id+"F2.wireOp",EDGE,"E6"),sQuery(id+"F2.wireOp",EDGE,"E7")])]}),"instanceName":"19"})});
            var Q39;
            Q39=makeQuery(id+"F6.opBoolean","COPY",EDGE,{"derivedFrom":makeQuery(id+"F5.opBoolean","INTERSECT",EDGE,{"derivedFrom":[makeQuery(id+"F4.opPattern","COPY",FACE,{"derivedFrom":makeQuery(id+"F3.opExtrude","SWEPT_FACE",FACE,{"disambiguationData":[OSD([sQuery(id+"F2.wireOp",EDGE,"E6")])]}),"instanceName":"18"}),makeQuery(id+"F4.opPattern","COPY",FACE,{"derivedFrom":makeQuery(id+"F3.opExtrude","SWEPT_FACE",FACE,{"disambiguationData":[OSD([sQuery(id+"F2.wireOp",EDGE,"E7")])]}),"instanceName":"19"})]})});
            var Q40;
            Q40=makeQuery(id+"F6.opBoolean","COPY",EDGE,{"derivedFrom":makeQuery(id+"F4.opPattern","COPY",EDGE,{"derivedFrom":makeQuery(id+"F3.opExtrude","SWEPT_EDGE",EDGE,{"disambiguationData":[OSD([sQuery(id+"F2.wireOp",EDGE,"E6"),sQuery(id+"F2.wireOp",EDGE,"E7")])]}),"instanceName":"18"})});
            var Q41;
            Q41=makeQuery(id+"F6.opBoolean","COPY",EDGE,{"derivedFrom":makeQuery(id+"F5.opBoolean","INTERSECT",EDGE,{"derivedFrom":[makeQuery(id+"F4.opPattern","COPY",FACE,{"derivedFrom":makeQuery(id+"F3.opExtrude","SWEPT_FACE",FACE,{"disambiguationData":[OSD([sQuery(id+"F2.wireOp",EDGE,"E6")])]}),"instanceName":"17"}),makeQuery(id+"F4.opPattern","COPY",FACE,{"derivedFrom":makeQuery(id+"F3.opExtrude","SWEPT_FACE",FACE,{"disambiguationData":[OSD([sQuery(id+"F2.wireOp",EDGE,"E7")])]}),"instanceName":"18"})]})});
            var Q42;
            Q42=makeQuery(id+"F6.opBoolean","COPY",EDGE,{"derivedFrom":makeQuery(id+"F4.opPattern","COPY",EDGE,{"derivedFrom":makeQuery(id+"F3.opExtrude","SWEPT_EDGE",EDGE,{"disambiguationData":[OSD([sQuery(id+"F2.wireOp",EDGE,"E6"),sQuery(id+"F2.wireOp",EDGE,"E7")])]}),"instanceName":"17"})});
            var Q43;
            Q43=makeQuery(id+"F6.opBoolean","COPY",EDGE,{"derivedFrom":makeQuery(id+"F5.opBoolean","INTERSECT",EDGE,{"derivedFrom":[makeQuery(id+"F4.opPattern","COPY",FACE,{"derivedFrom":makeQuery(id+"F3.opExtrude","SWEPT_FACE",FACE,{"disambiguationData":[OSD([sQuery(id+"F2.wireOp",EDGE,"E6")])]}),"instanceName":"16"}),makeQuery(id+"F4.opPattern","COPY",FACE,{"derivedFrom":makeQuery(id+"F3.opExtrude","SWEPT_FACE",FACE,{"disambiguationData":[OSD([sQuery(id+"F2.wireOp",EDGE,"E7")])]}),"instanceName":"17"})]})});
            var Q44;
            Q44=makeQuery(id+"F6.opBoolean","COPY",EDGE,{"derivedFrom":makeQuery(id+"F4.opPattern","COPY",EDGE,{"derivedFrom":makeQuery(id+"F3.opExtrude","SWEPT_EDGE",EDGE,{"disambiguationData":[OSD([sQuery(id+"F2.wireOp",EDGE,"E6"),sQuery(id+"F2.wireOp",EDGE,"E7")])]}),"instanceName":"16"})});
            var Q45;
            Q45=makeQuery(id+"F6.opBoolean","COPY",EDGE,{"derivedFrom":makeQuery(id+"F5.opBoolean","INTERSECT",EDGE,{"derivedFrom":[makeQuery(id+"F4.opPattern","COPY",FACE,{"derivedFrom":makeQuery(id+"F3.opExtrude","SWEPT_FACE",FACE,{"disambiguationData":[OSD([sQuery(id+"F2.wireOp",EDGE,"E6")])]}),"instanceName":"15"}),makeQuery(id+"F4.opPattern","COPY",FACE,{"derivedFrom":makeQuery(id+"F3.opExtrude","SWEPT_FACE",FACE,{"disambiguationData":[OSD([sQuery(id+"F2.wireOp",EDGE,"E7")])]}),"instanceName":"16"})]})});
            var Q46;
            Q46=makeQuery(id+"F6.opBoolean","COPY",EDGE,{"derivedFrom":makeQuery(id+"F4.opPattern","COPY",EDGE,{"derivedFrom":makeQuery(id+"F3.opExtrude","SWEPT_EDGE",EDGE,{"disambiguationData":[OSD([sQuery(id+"F2.wireOp",EDGE,"E6"),sQuery(id+"F2.wireOp",EDGE,"E7")])]}),"instanceName":"15"})});
            var Q47;
            Q47=makeQuery(id+"F6.opBoolean","COPY",EDGE,{"derivedFrom":makeQuery(id+"F4.opPattern","COPY",EDGE,{"derivedFrom":makeQuery(id+"F3.opExtrude","SWEPT_EDGE",EDGE,{"disambiguationData":[OSD([sQuery(id+"F2.wireOp",EDGE,"E6"),sQuery(id+"F2.wireOp",EDGE,"E7")])]}),"instanceName":"14"})});
            var Q48;
            Q48=makeQuery(id+"F6.opBoolean","COPY",EDGE,{"derivedFrom":makeQuery(id+"F5.opBoolean","INTERSECT",EDGE,{"derivedFrom":[makeQuery(id+"F4.opPattern","COPY",FACE,{"derivedFrom":makeQuery(id+"F3.opExtrude","SWEPT_FACE",FACE,{"disambiguationData":[OSD([sQuery(id+"F2.wireOp",EDGE,"E6")])]}),"instanceName":"15"}),makeQuery(id+"F4.opPattern","COPY",FACE,{"derivedFrom":makeQuery(id+"F3.opExtrude","SWEPT_FACE",FACE,{"disambiguationData":[OSD([sQuery(id+"F2.wireOp",EDGE,"E7")])]}),"instanceName":"16"})]})});
            var Q49;
            Q49=makeQuery(id+"F6.opBoolean","COPY",EDGE,{"derivedFrom":makeQuery(id+"F4.opPattern","COPY",EDGE,{"derivedFrom":makeQuery(id+"F3.opExtrude","SWEPT_EDGE",EDGE,{"disambiguationData":[OSD([sQuery(id+"F2.wireOp",EDGE,"E6"),sQuery(id+"F2.wireOp",EDGE,"E7")])]}),"instanceName":"15"})});
            var Q50;
            Q50=makeQuery(id+"F6.opBoolean","COPY",EDGE,{"derivedFrom":makeQuery(id+"F5.opBoolean","INTERSECT",EDGE,{"derivedFrom":[makeQuery(id+"F4.opPattern","COPY",FACE,{"derivedFrom":makeQuery(id+"F3.opExtrude","SWEPT_FACE",FACE,{"disambiguationData":[OSD([sQuery(id+"F2.wireOp",EDGE,"E6")])]}),"instanceName":"13"}),makeQuery(id+"F4.opPattern","COPY",FACE,{"derivedFrom":makeQuery(id+"F3.opExtrude","SWEPT_FACE",FACE,{"disambiguationData":[OSD([sQuery(id+"F2.wireOp",EDGE,"E7")])]}),"instanceName":"14"})]})});
            var Q51;
            Q51=makeQuery(id+"F6.opBoolean","COPY",EDGE,{"derivedFrom":makeQuery(id+"F5.opBoolean","INTERSECT",EDGE,{"derivedFrom":[makeQuery(id+"F4.opPattern","COPY",FACE,{"derivedFrom":makeQuery(id+"F3.opExtrude","SWEPT_FACE",FACE,{"disambiguationData":[OSD([sQuery(id+"F2.wireOp",EDGE,"E6")])]}),"instanceName":"14"}),makeQuery(id+"F4.opPattern","COPY",FACE,{"derivedFrom":makeQuery(id+"F3.opExtrude","SWEPT_FACE",FACE,{"disambiguationData":[OSD([sQuery(id+"F2.wireOp",EDGE,"E7")])]}),"instanceName":"15"})]})});
            var Q52;
            Q52=makeQuery(id+"F6.opBoolean","COPY",EDGE,{"derivedFrom":makeQuery(id+"F4.opPattern","COPY",EDGE,{"derivedFrom":makeQuery(id+"F3.opExtrude","SWEPT_EDGE",EDGE,{"disambiguationData":[OSD([sQuery(id+"F2.wireOp",EDGE,"E6"),sQuery(id+"F2.wireOp",EDGE,"E7")])]}),"instanceName":"13"})});
            var Q53;
            Q53=makeQuery(id+"F6.opBoolean","COPY",EDGE,{"derivedFrom":makeQuery(id+"F5.opBoolean","INTERSECT",EDGE,{"derivedFrom":[makeQuery(id+"F4.opPattern","COPY",FACE,{"derivedFrom":makeQuery(id+"F3.opExtrude","SWEPT_FACE",FACE,{"disambiguationData":[OSD([sQuery(id+"F2.wireOp",EDGE,"E6")])]}),"instanceName":"12"}),makeQuery(id+"F4.opPattern","COPY",FACE,{"derivedFrom":makeQuery(id+"F3.opExtrude","SWEPT_FACE",FACE,{"disambiguationData":[OSD([sQuery(id+"F2.wireOp",EDGE,"E7")])]}),"instanceName":"13"})]})});
            var Q54;
            Q54=makeQuery(id+"F6.opBoolean","COPY",EDGE,{"derivedFrom":makeQuery(id+"F4.opPattern","COPY",EDGE,{"derivedFrom":makeQuery(id+"F3.opExtrude","SWEPT_EDGE",EDGE,{"disambiguationData":[OSD([sQuery(id+"F2.wireOp",EDGE,"E6"),sQuery(id+"F2.wireOp",EDGE,"E7")])]}),"instanceName":"12"})});
            var Q55;
            Q55=makeQuery(id+"F6.opBoolean","COPY",EDGE,{"derivedFrom":makeQuery(id+"F5.opBoolean","INTERSECT",EDGE,{"derivedFrom":[makeQuery(id+"F4.opPattern","COPY",FACE,{"derivedFrom":makeQuery(id+"F3.opExtrude","SWEPT_FACE",FACE,{"disambiguationData":[OSD([sQuery(id+"F2.wireOp",EDGE,"E6")])]}),"instanceName":"11"}),makeQuery(id+"F4.opPattern","COPY",FACE,{"derivedFrom":makeQuery(id+"F3.opExtrude","SWEPT_FACE",FACE,{"disambiguationData":[OSD([sQuery(id+"F2.wireOp",EDGE,"E7")])]}),"instanceName":"12"})]})});
            var Q56;
            Q56=makeQuery(id+"F6.opBoolean","COPY",EDGE,{"derivedFrom":makeQuery(id+"F4.opPattern","COPY",EDGE,{"derivedFrom":makeQuery(id+"F3.opExtrude","SWEPT_EDGE",EDGE,{"disambiguationData":[OSD([sQuery(id+"F2.wireOp",EDGE,"E6"),sQuery(id+"F2.wireOp",EDGE,"E7")])]}),"instanceName":"11"})});
            var Q57;
            Q57=makeQuery(id+"F6.opBoolean","COPY",EDGE,{"derivedFrom":makeQuery(id+"F5.opBoolean","INTERSECT",EDGE,{"derivedFrom":[makeQuery(id+"F4.opPattern","COPY",FACE,{"derivedFrom":makeQuery(id+"F3.opExtrude","SWEPT_FACE",FACE,{"disambiguationData":[OSD([sQuery(id+"F2.wireOp",EDGE,"E6")])]}),"instanceName":"10"}),makeQuery(id+"F4.opPattern","COPY",FACE,{"derivedFrom":makeQuery(id+"F3.opExtrude","SWEPT_FACE",FACE,{"disambiguationData":[OSD([sQuery(id+"F2.wireOp",EDGE,"E7")])]}),"instanceName":"11"})]})});
            var Q58;
            Q58=makeQuery(id+"F6.opBoolean","COPY",EDGE,{"derivedFrom":makeQuery(id+"F4.opPattern","COPY",EDGE,{"derivedFrom":makeQuery(id+"F3.opExtrude","SWEPT_EDGE",EDGE,{"disambiguationData":[OSD([sQuery(id+"F2.wireOp",EDGE,"E6"),sQuery(id+"F2.wireOp",EDGE,"E7")])]}),"instanceName":"10"})});
            var Q59;
            Q59=makeQuery(id+"F6.opBoolean","COPY",EDGE,{"derivedFrom":makeQuery(id+"F5.opBoolean","INTERSECT",EDGE,{"derivedFrom":[makeQuery(id+"F4.opPattern","COPY",FACE,{"derivedFrom":makeQuery(id+"F3.opExtrude","SWEPT_FACE",FACE,{"disambiguationData":[OSD([sQuery(id+"F2.wireOp",EDGE,"E6")])]}),"instanceName":"9"}),makeQuery(id+"F4.opPattern","COPY",FACE,{"derivedFrom":makeQuery(id+"F3.opExtrude","SWEPT_FACE",FACE,{"disambiguationData":[OSD([sQuery(id+"F2.wireOp",EDGE,"E7")])]}),"instanceName":"10"})]})});
            var Q60;
            Q60=makeQuery(id+"F6.opBoolean","COPY",EDGE,{"derivedFrom":makeQuery(id+"F4.opPattern","COPY",EDGE,{"derivedFrom":makeQuery(id+"F3.opExtrude","SWEPT_EDGE",EDGE,{"disambiguationData":[OSD([sQuery(id+"F2.wireOp",EDGE,"E6"),sQuery(id+"F2.wireOp",EDGE,"E7")])]}),"instanceName":"9"})});
            var Q61;
            Q61=makeQuery(id+"F6.opBoolean","COPY",EDGE,{"derivedFrom":makeQuery(id+"F5.opBoolean","INTERSECT",EDGE,{"derivedFrom":[makeQuery(id+"F4.opPattern","COPY",FACE,{"derivedFrom":makeQuery(id+"F3.opExtrude","SWEPT_FACE",FACE,{"disambiguationData":[OSD([sQuery(id+"F2.wireOp",EDGE,"E6")])]}),"instanceName":"8"}),makeQuery(id+"F4.opPattern","COPY",FACE,{"derivedFrom":makeQuery(id+"F3.opExtrude","SWEPT_FACE",FACE,{"disambiguationData":[OSD([sQuery(id+"F2.wireOp",EDGE,"E7")])]}),"instanceName":"9"})]})});
            var Q62;
            Q62=makeQuery(id+"F6.opBoolean","COPY",EDGE,{"derivedFrom":makeQuery(id+"F4.opPattern","COPY",EDGE,{"derivedFrom":makeQuery(id+"F3.opExtrude","SWEPT_EDGE",EDGE,{"disambiguationData":[OSD([sQuery(id+"F2.wireOp",EDGE,"E6"),sQuery(id+"F2.wireOp",EDGE,"E7")])]}),"instanceName":"8"})});
            var Q63;
            Q63=makeQuery(id+"F6.opBoolean","COPY",EDGE,{"derivedFrom":makeQuery(id+"F5.opBoolean","INTERSECT",EDGE,{"derivedFrom":[makeQuery(id+"F4.opPattern","COPY",FACE,{"derivedFrom":makeQuery(id+"F3.opExtrude","SWEPT_FACE",FACE,{"disambiguationData":[OSD([sQuery(id+"F2.wireOp",EDGE,"E6")])]}),"instanceName":"7"}),makeQuery(id+"F4.opPattern","COPY",FACE,{"derivedFrom":makeQuery(id+"F3.opExtrude","SWEPT_FACE",FACE,{"disambiguationData":[OSD([sQuery(id+"F2.wireOp",EDGE,"E7")])]}),"instanceName":"8"})]})});
            var Q64;
            Q64=makeQuery(id+"F6.opBoolean","COPY",EDGE,{"derivedFrom":makeQuery(id+"F4.opPattern","COPY",EDGE,{"derivedFrom":makeQuery(id+"F3.opExtrude","SWEPT_EDGE",EDGE,{"disambiguationData":[OSD([sQuery(id+"F2.wireOp",EDGE,"E6"),sQuery(id+"F2.wireOp",EDGE,"E7")])]}),"instanceName":"7"})});
            var Q65;
            Q65=makeQuery(id+"F6.opBoolean","COPY",EDGE,{"derivedFrom":makeQuery(id+"F5.opBoolean","INTERSECT",EDGE,{"derivedFrom":[makeQuery(id+"F4.opPattern","COPY",FACE,{"derivedFrom":makeQuery(id+"F3.opExtrude","SWEPT_FACE",FACE,{"disambiguationData":[OSD([sQuery(id+"F2.wireOp",EDGE,"E6")])]}),"instanceName":"6"}),makeQuery(id+"F4.opPattern","COPY",FACE,{"derivedFrom":makeQuery(id+"F3.opExtrude","SWEPT_FACE",FACE,{"disambiguationData":[OSD([sQuery(id+"F2.wireOp",EDGE,"E7")])]}),"instanceName":"7"})]})});
            fillet(context, id + "F7", {"entities" : qUnion([Q0, Q1, Q2, Q3, Q4, Q5, Q6, Q7, Q8, Q9, Q10, Q11, Q12, Q13, Q14, Q15, Q16, Q17, Q18, Q19, Q20, Q21, Q22, Q23, Q24, Q25, Q26, Q27, Q28, Q29, Q30, Q31, Q32, Q33, Q34, Q35, Q36, Q37, Q38, Q39, Q40, Q41, Q42, Q43, Q44, Q45, Q46, Q47, Q48, Q49, Q50, Q51, Q52, Q53, Q54, Q55, Q56, Q57, Q58, Q59, Q60, Q61, Q62, Q63, Q64, Q65]), "radius" : 0.4 * mm, "tangentPropagation" : true, "rho" : .3, "crossSection" : FilletCrossSection.CONIC, "allowEdgeOverflow" : false});
        }
    });
